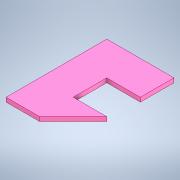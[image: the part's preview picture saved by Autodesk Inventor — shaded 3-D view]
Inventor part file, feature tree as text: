
AUTODESK INVENTOR PART (.ipt)
format: ipt  version: 2020 (Build 240168000, 168)  size: 99,328 bytes
history: native  units: in
note: dims shown in document units (in); Inventor stores cm internally (conversion verified against a paired STEP export)
features: extrude x1, sketch x1
ambient origin geometry x8: Origin, YZ Plane, XZ Plane, XY Plane, X Axis, Y Axis, Z Axis, Center Point
bodies: Solid1 (feature_tree)
feature tree (2):
  extrude  "Extrusion1"  Depth=1.0in
  sketch  "Sketch1"  dims[d0=0.5in d1=1.0in d2=0.5in d4=0.063in d5=0.0in]
